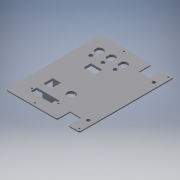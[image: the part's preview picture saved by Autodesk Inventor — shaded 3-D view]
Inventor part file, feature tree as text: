
AUTODESK INVENTOR PART (.ipt)
format: ipt  version: 2016 (Build 200138000, 138)  size: 318,976 bytes
history: native  units: in
note: dims shown in document units (in); Inventor stores cm internally (conversion verified against a paired STEP export)
features: extrude x7, sketch x7, fillet x1
ambient origin geometry x8: Origin, YZ Plane, XZ Plane, XY Plane, X Axis, Y Axis, Z Axis, Center Point
bodies: Solid1 (feature_tree)
feature tree (15):
  extrude  "Extrusion1"  Depth=0.6299in
  extrude  "Extrusion2"  Depth=6.5354in
  extrude  "Extrusion8"  Depth=1.063in
  fillet  "Fillet1"  Radius=0.0394in
  extrude  "Extrusion9"  Depth=0.0394in
  extrude  "Extrusion10"  Depth=0.0394in
  extrude  "Extrusion11"  Depth=0.1181in
  extrude  "Extrusion12"  Depth=0.1181in
  sketch  "Sketch1"  dims[d0=0.9449in d1=0.6299in]
  sketch  "Sketch2"  dims[d2=3.4612in d3=6.5354in]
  sketch  "Sketch9"  dims[d4=0.1181in d5=1.063in d6=0.0394in]
  sketch  "Sketch10"  dims[d8=0.0394in d9=0.0394in]
  sketch  "Sketch11"  dims[d10=0.0394in d11=0.0394in]
  sketch  "Sketch12"  dims[d12=0.0787in d13=0.0in d14=0.1181in]
  sketch  "Sketch15"  dims[d15=0.1181in d16=0.1181in d17=0.2756in d18=0.1181in d19=0.1181in d20=0.0787in d21=0.0in d62=0.1181in d63=0.2362in d64=0.1181in d65=0.5315in d66=0.7874in d67=1.1811in d69=0.7874in d70=0.6693in d71=0.5709in d72=0.5512in d75=0.5512in d76=0.5512in d77=0.5512in d78=0.8583in d79=0.8583in d80=0.2559in d81=0.2559in d82=0.2559in d83=0.5906in d84=0.5906in d85=0.5906in d89=0.8583in d90=0.8583in d92=0.8583in d93=0.8583in d97=0.4331in d98=1.6339in d99=0.2953in d100=0.1181in d101=0.1181in d102=0.1181in d103=0.1181in d104=0.5906in d105=0.0in d106=1.0177in d108=0.0in d109=0.8071in d111=0.1181in d112=0.0787in d113=0.0787in d114=0.0787in d115=0.6693in d116=0.0in d117=0.0787in d118=0.0787in d120=0.0315in d121=0.0315in d122=0.315in d123=0.0in d124=0.0787in d126=0.126in d127=0.0591in d128=0.315in d129=0.0in d130=0.2008in d131=4.3307in d132=1.1811in d133=0.0787in d134=0.0in]
